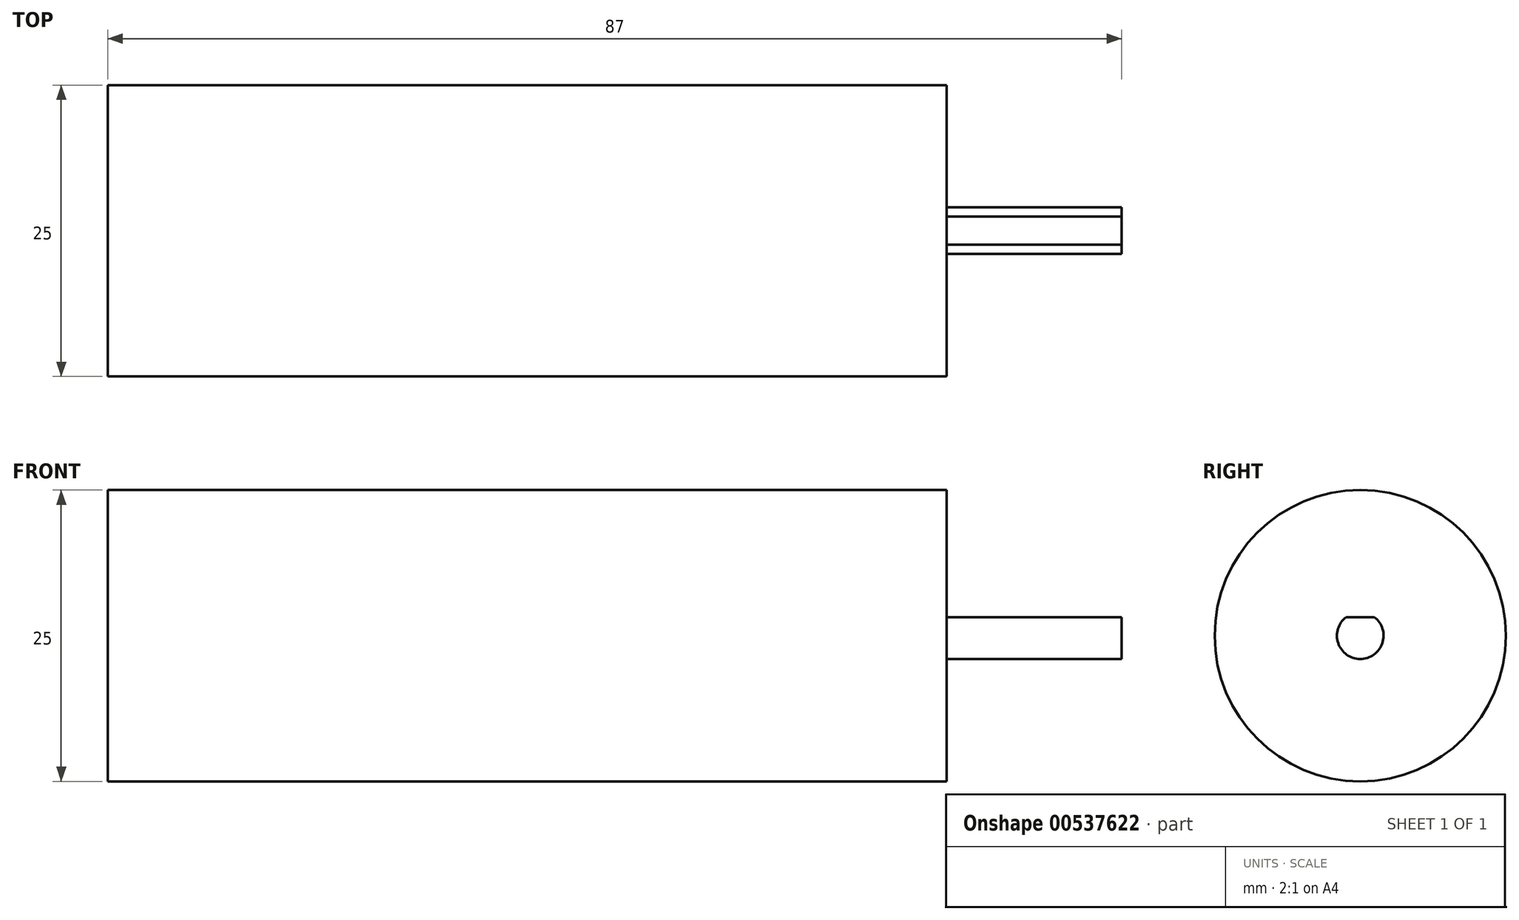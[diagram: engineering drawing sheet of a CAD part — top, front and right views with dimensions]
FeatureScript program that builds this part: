
annotation { "Feature Type Name" : "Feature", "Feature Type Description" : "" }
export const myFeature = defineFeature(function(context is Context, id is Id, definition is map)
    precondition{}
    {
        {
            var Q0;
            Q0=qCreatedBy(makeId("Right.planeOp"),FACE);
            var sketch = newSketch(context, id + "F0", { "sketchPlane" : qUnion([Q0])});
            skCircle(sketch, "E0", {"center": v(0, 0) * mm, "radius": 12.5 * mm});
            skSolve(sketch);
        }
        {
            var Q0;
            Q0=makeQuery(id+"F0.imprint","IMPRINT",FACE,{"disambiguationData":[TD([[makeQuery(id+"F0.imprint","IMPRINT",EDGE,{"derivedFrom":sQuery(id+"F0.wireOp",EDGE,"E0")}),1.0]])]});
            extrude(context, id + "F1", {"entities" : qUnion([Q0]), "depth" : 72 * mm, "offsetDistance" : 25 * mm});
        }
        {
            var Q0;
            Q0=makeQuery(id+"F1.opExtrude","CAP_FACE",FACE,{"disambiguationData":[OSD([sQuery(id+"F0.wireOp",EDGE,"E0")])],"isStart":false});
            var sketch = newSketch(context, id + "F2", { "sketchPlane" : qUnion([Q0])});
            skArc(sketch, "E1", {"start": v(-1.2, 1.6) * mm, "mid": v(0, -2) * mm, "end": v(1.2, 1.6) * mm});
            skLineSegment(sketch, "E2", {"start": v(-1.2, 1.6) * mm, "end": v(1.2, 1.6) * mm});
            skSolve(sketch);
        }
        {
            var Q0;
            Q0=makeQuery(id+"F2.imprint","IMPRINT",FACE,{"disambiguationData":[TD([[makeQuery(id+"F2.imprint","IMPRINT",EDGE,{"derivedFrom":sQuery(id+"F2.wireOp",EDGE,"E1")}),1.0]])]});
            extrude(context, id + "F3", {"entities" : qUnion([Q0]), "operationType" : NewBodyOperationType.ADD, "depth" : 15 * mm, "offsetDistance" : 25 * mm});
        }
    });
